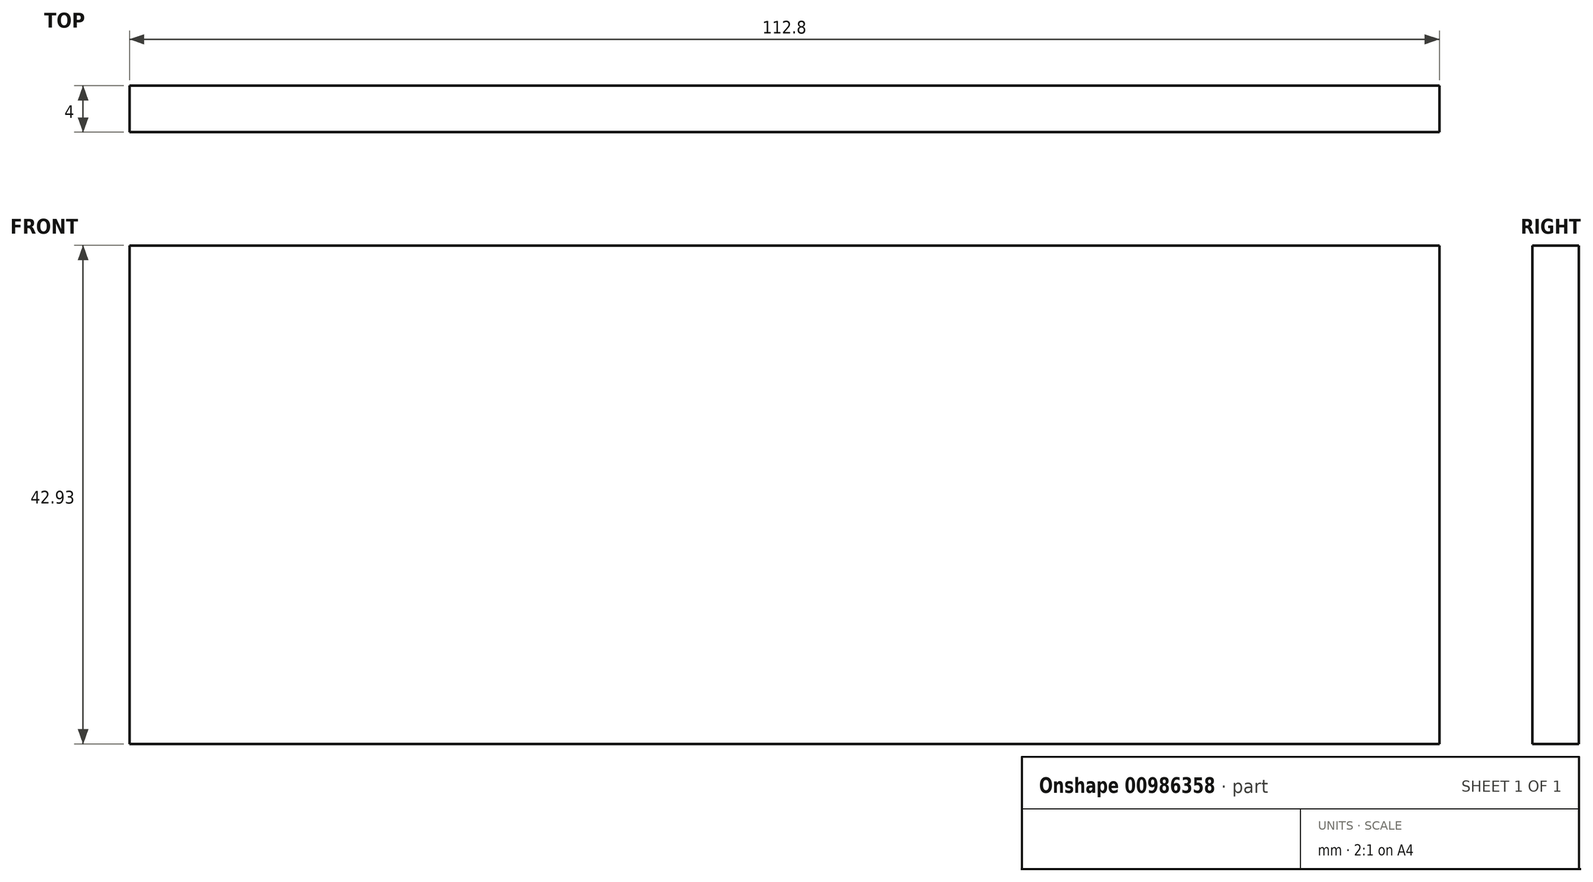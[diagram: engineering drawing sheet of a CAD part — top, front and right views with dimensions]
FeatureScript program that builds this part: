
annotation { "Feature Type Name" : "Feature", "Feature Type Description" : "" }
export const myFeature = defineFeature(function(context is Context, id is Id, definition is map)
    precondition{}
    {
        {
            var Q0;
            Q0=qCreatedBy(makeId("Front.planeOp"),FACE);
            var sketch = newSketch(context, id + "F0", { "sketchPlane" : qUnion([Q0])});
            skLineSegment(sketch, "E0.bottom", {"start": v(-49.59, -17.32) * mm, "end": v(63.2, -17.32) * mm});
            skLineSegment(sketch, "E0.top", {"start": v(-49.59, 25.6) * mm, "end": v(63.2, 25.6) * mm});
            skLineSegment(sketch, "E0.left", {"start": v(-49.59, -17.32) * mm, "end": v(-49.59, 25.6) * mm});
            skLineSegment(sketch, "E0.right", {"start": v(63.2, -17.32) * mm, "end": v(63.2, 25.6) * mm});
            skSolve(sketch);
        }
        {
            var Q0;
            Q0=makeQuery(id+"F0.imprint","IMPRINT",FACE,{"disambiguationData":[TD([[makeQuery(id+"F0.imprint","IMPRINT",EDGE,{"derivedFrom":sQuery(id+"F0.wireOp",EDGE,"E0.bottom")}),1.0]])]});
            extrude(context, id + "F1", {"entities" : qUnion([Q0]), "depth" : 4 * mm, "offsetDistance" : 25 * mm});
        }
    });
